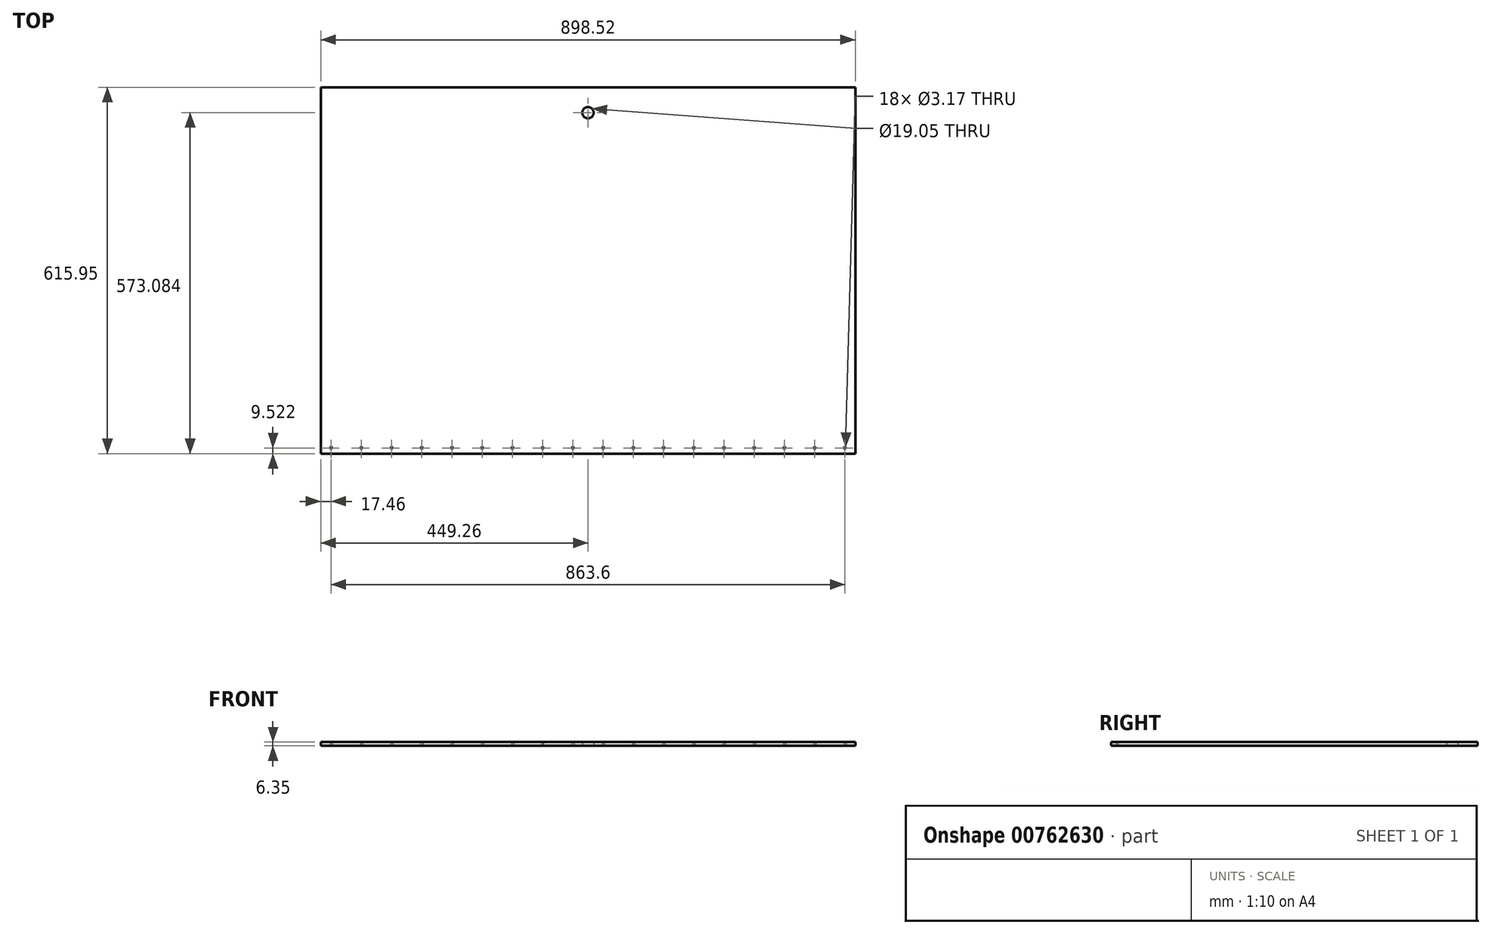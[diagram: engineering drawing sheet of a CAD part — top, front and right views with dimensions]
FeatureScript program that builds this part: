
annotation { "Feature Type Name" : "Feature", "Feature Type Description" : "" }
export const myFeature = defineFeature(function(context is Context, id is Id, definition is map)
    precondition{}
    {
        {
            var Q0;
            Q0=qCreatedBy(makeId("Top.planeOp"),FACE);
            var sketch = newSketch(context, id + "F0", { "sketchPlane" : qUnion([Q0])});
            skLineSegment(sketch, "E0.bottom", {"start": v(-449.26, 241.9) * mm, "end": v(449.26, 241.9) * mm});
            skLineSegment(sketch, "E0.top", {"start": v(-449.26, -374.04) * mm, "end": v(449.26, -374.04) * mm});
            skLineSegment(sketch, "E0.left", {"start": v(-449.26, 241.9) * mm, "end": v(-449.26, -374.04) * mm});
            skLineSegment(sketch, "E0.right", {"start": v(449.26, 241.9) * mm, "end": v(449.26, -374.04) * mm});
            skCircle(sketch, "E1", {"center": v(0, 199.04) * mm, "radius": 9.52 * mm});
            skCircle(sketch, "E2", {"center": v(-431.8, -364.52) * mm, "radius": 1.59 * mm});
            skCircle(sketch, "E3.1.0.0", {"center": v(-381, -364.52) * mm, "radius": 1.59 * mm});
            skCircle(sketch, "E3.2.0.0", {"center": v(-330.2, -364.52) * mm, "radius": 1.59 * mm});
            skCircle(sketch, "E3.3.0.0", {"center": v(-279.4, -364.52) * mm, "radius": 1.59 * mm});
            skCircle(sketch, "E3.4.0.0", {"center": v(-228.6, -364.52) * mm, "radius": 1.59 * mm});
            skCircle(sketch, "E3.5.0.0", {"center": v(-177.8, -364.52) * mm, "radius": 1.59 * mm});
            skCircle(sketch, "E3.6.0.0", {"center": v(-127, -364.52) * mm, "radius": 1.59 * mm});
            skCircle(sketch, "E3.7.0.0", {"center": v(-76.2, -364.52) * mm, "radius": 1.59 * mm});
            skCircle(sketch, "E3.8.0.0", {"center": v(-25.4, -364.52) * mm, "radius": 1.59 * mm});
            skCircle(sketch, "E3.9.0.0", {"center": v(25.4, -364.52) * mm, "radius": 1.59 * mm});
            skCircle(sketch, "E3.10.0.0", {"center": v(76.2, -364.52) * mm, "radius": 1.59 * mm});
            skCircle(sketch, "E3.11.0.0", {"center": v(127, -364.52) * mm, "radius": 1.59 * mm});
            skCircle(sketch, "E3.12.0.0", {"center": v(177.8, -364.52) * mm, "radius": 1.59 * mm});
            skCircle(sketch, "E3.13.0.0", {"center": v(228.6, -364.52) * mm, "radius": 1.59 * mm});
            skCircle(sketch, "E3.14.0.0", {"center": v(279.4, -364.52) * mm, "radius": 1.59 * mm});
            skCircle(sketch, "E3.15.0.0", {"center": v(330.2, -364.52) * mm, "radius": 1.59 * mm});
            skCircle(sketch, "E3.16.0.0", {"center": v(381, -364.52) * mm, "radius": 1.59 * mm});
            skCircle(sketch, "E3.17.0.0", {"center": v(431.8, -364.52) * mm, "radius": 1.59 * mm});
            skLineSegment(sketch, "E3.direction1", {"start": v(-431.8, -364.52) * mm, "end": v(-381, -364.52) * mm, "construction": true});
            skSolve(sketch);
        }
        {
            var Q0;
            Q0=makeQuery(id+"F0.imprint","IMPRINT",FACE,{"disambiguationData":[TD([[makeQuery(id+"F0.imprint","IMPRINT",EDGE,{"derivedFrom":sQuery(id+"F0.wireOp",EDGE,"E0.bottom")}),-1.0]])]});
            extrude(context, id + "F1", {"entities" : qUnion([Q0]), "depth" : 6.35 * mm, "offsetDistance" : 25.4 * mm});
        }
    });
